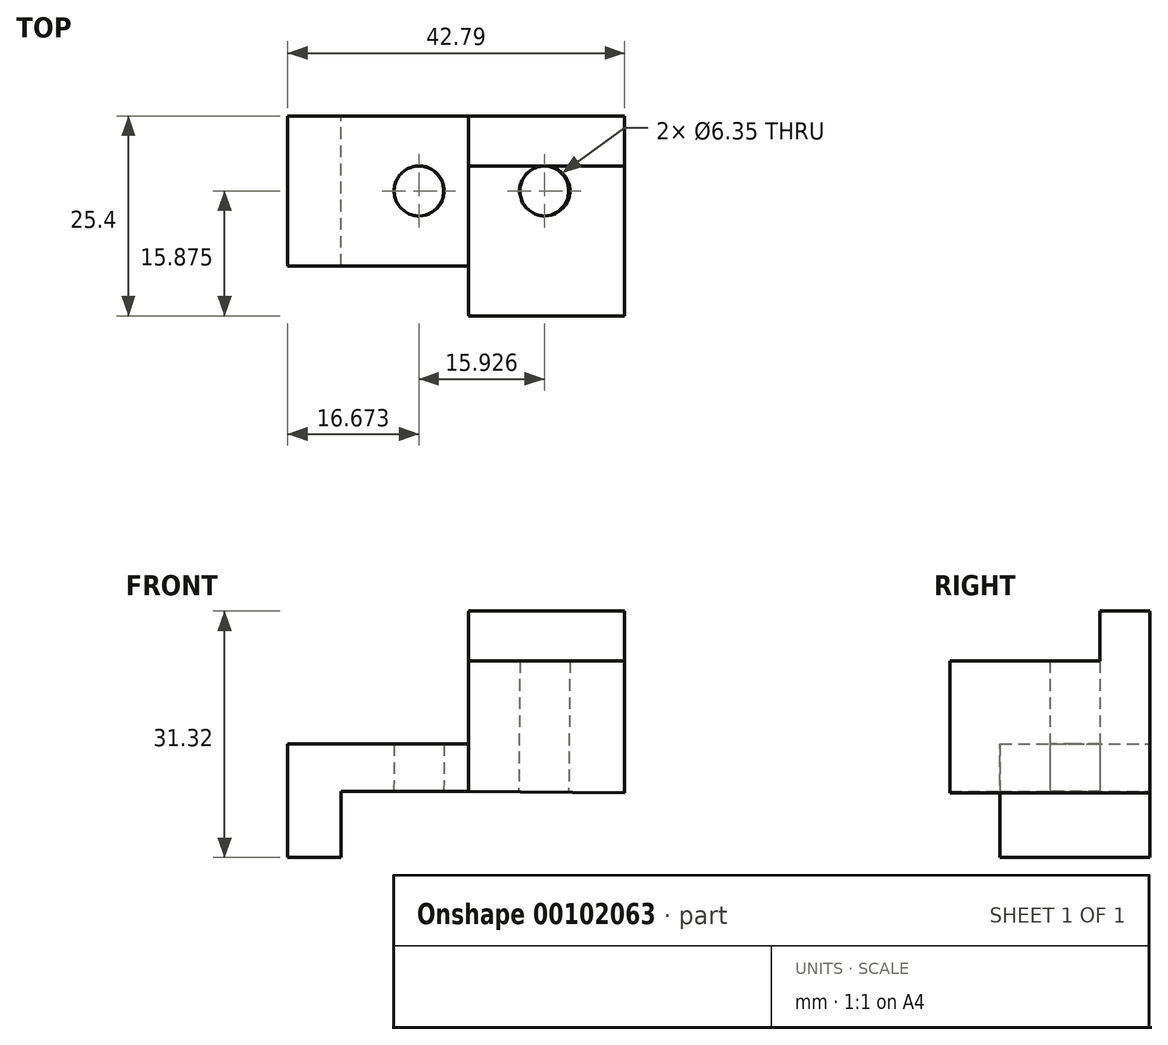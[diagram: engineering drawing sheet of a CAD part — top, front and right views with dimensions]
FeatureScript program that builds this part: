
annotation { "Feature Type Name" : "Feature", "Feature Type Description" : "" }
export const myFeature = defineFeature(function(context is Context, id is Id, definition is map)
    precondition{}
    {
        {
            var Q0;
            Q0=qCreatedBy(makeId("Front.planeOp"),FACE);
            var sketch = newSketch(context, id + "F0", { "sketchPlane" : qUnion([Q0])});
            skLineSegment(sketch, "E0", {"start": v(0, 0) * mm, "end": v(0, 14.42) * mm});
            skLineSegment(sketch, "E1", {"start": v(0, 14.42) * mm, "end": v(23, 14.42) * mm});
            skLineSegment(sketch, "E2", {"start": v(23, 14.42) * mm, "end": v(23, 8.39) * mm});
            skLineSegment(sketch, "E3", {"start": v(23, 8.39) * mm, "end": v(6.79, 8.39) * mm});
            skLineSegment(sketch, "E4", {"start": v(6.79, 8.39) * mm, "end": v(6.79, 0) * mm});
            skLineSegment(sketch, "E5", {"start": v(6.79, 0) * mm, "end": v(0, 0) * mm});
            skLineSegment(sketch, "E6", {"start": v(23, 8.39) * mm, "end": v(23, 24.97) * mm});
            skLineSegment(sketch, "E7", {"start": v(23, 24.97) * mm, "end": v(42.79, 24.97) * mm});
            skLineSegment(sketch, "E8", {"start": v(42.79, 24.97) * mm, "end": v(42.79, 8.2) * mm});
            skLineSegment(sketch, "E9", {"start": v(42.79, 8.2) * mm, "end": v(23, 8.39) * mm});
            skSolve(sketch);
        }
        {
            var Q0;
            Q0=makeQuery(id+"F0.imprint","IMPRINT",FACE,{"disambiguationData":[TD([[makeQuery(id+"F0.imprint","IMPRINT",EDGE,{"derivedFrom":sQuery(id+"F0.wireOp",EDGE,"E0")}),-1.0]])]});
            extrude(context, id + "F1", {"entities" : qUnion([Q0]), "depth" : 19.05 * mm});
        }
        {
            var Q0;
            {var subQ0=sQuery(id+"F0.wireOp",EDGE,"E7");Q0=makeQuery(id+"F0.imprint","IMPRINT",FACE,{"disambiguationData":[TD([[makeQuery(id+"F0.imprint","IMPRINT",EDGE,{"derivedFrom":subQ0}),-1.0]])]});}
            extrude(context, id + "F2", {"entities" : qUnion([Q0]), "operationType" : NewBodyOperationType.ADD, "depth" : 25.4 * mm});
        }
        {
            var Q0;
            Q0=makeQuery(id+"F2.opExtrude","SWEPT_FACE",FACE,{"disambiguationData":[OSD([sQuery(id+"F0.wireOp",EDGE,"E7")])]});
            var sketch = newSketch(context, id + "F3", { "sketchPlane" : qUnion([Q0])});
            skLineSegment(sketch, "E10", {"start": v(42.79, 0) * mm, "end": v(42.79, -6.35) * mm});
            skLineSegment(sketch, "E11", {"start": v(42.79, -6.35) * mm, "end": v(23, -6.35) * mm});
            skLineSegment(sketch, "E12", {"start": v(23, -6.35) * mm, "end": v(23, 0) * mm});
            skLineSegment(sketch, "E13", {"start": v(23, 0) * mm, "end": v(42.79, 0) * mm});
            skSolve(sketch);
        }
        {
            var Q0;
            Q0=makeQuery(id+"F3.imprint","IMPRINT",FACE,{"disambiguationData":[TD([[makeQuery(id+"F3.imprint","IMPRINT",EDGE,{"derivedFrom":sQuery(id+"F3.wireOp",EDGE,"E10")}),1.0]])]});
            extrude(context, id + "F4", {"entities" : qUnion([Q0]), "operationType" : NewBodyOperationType.ADD, "depth" : 6.35 * mm});
        }
        {
            var Q0;
            Q0=makeQuery(id+"F2.opExtrude","SWEPT_FACE",FACE,{"disambiguationData":[OSD([sQuery(id+"F0.wireOp",EDGE,"E9")])]});
            var sketch = newSketch(context, id + "F5", { "sketchPlane" : qUnion([Q0])});
            skLineSegment(sketch, "E14", {"start": v(22.91, 0) * mm, "end": v(32.44, 0) * mm, "construction": true});
            skLineSegment(sketch, "E15", {"start": v(32.44, 0) * mm, "end": v(32.44, 9.53) * mm, "construction": true});
            skLineSegment(sketch, "E16", {"start": v(22.91, 0) * mm, "end": v(16.56, 0) * mm, "construction": true});
            skLineSegment(sketch, "E17", {"start": v(16.56, 0) * mm, "end": v(16.56, 9.53) * mm, "construction": true});
            skCircle(sketch, "E18", {"center": v(16.56, 9.53) * mm, "radius": 3.18 * mm});
            skCircle(sketch, "E19", {"center": v(32.44, 9.53) * mm, "radius": 3.18 * mm});
            skSolve(sketch);
        }
        {
            var Q0;
            Q0 = qSketchRegion(id + "F5", true);
            extrude(context, id + "F6", {"entities" : qUnion([Q0]), "operationType" : NewBodyOperationType.REMOVE, "endBound" : BoundingType.SYMMETRIC, "oppositeDirection" : true, "depth" : 38.1 * mm});
        }
    });
